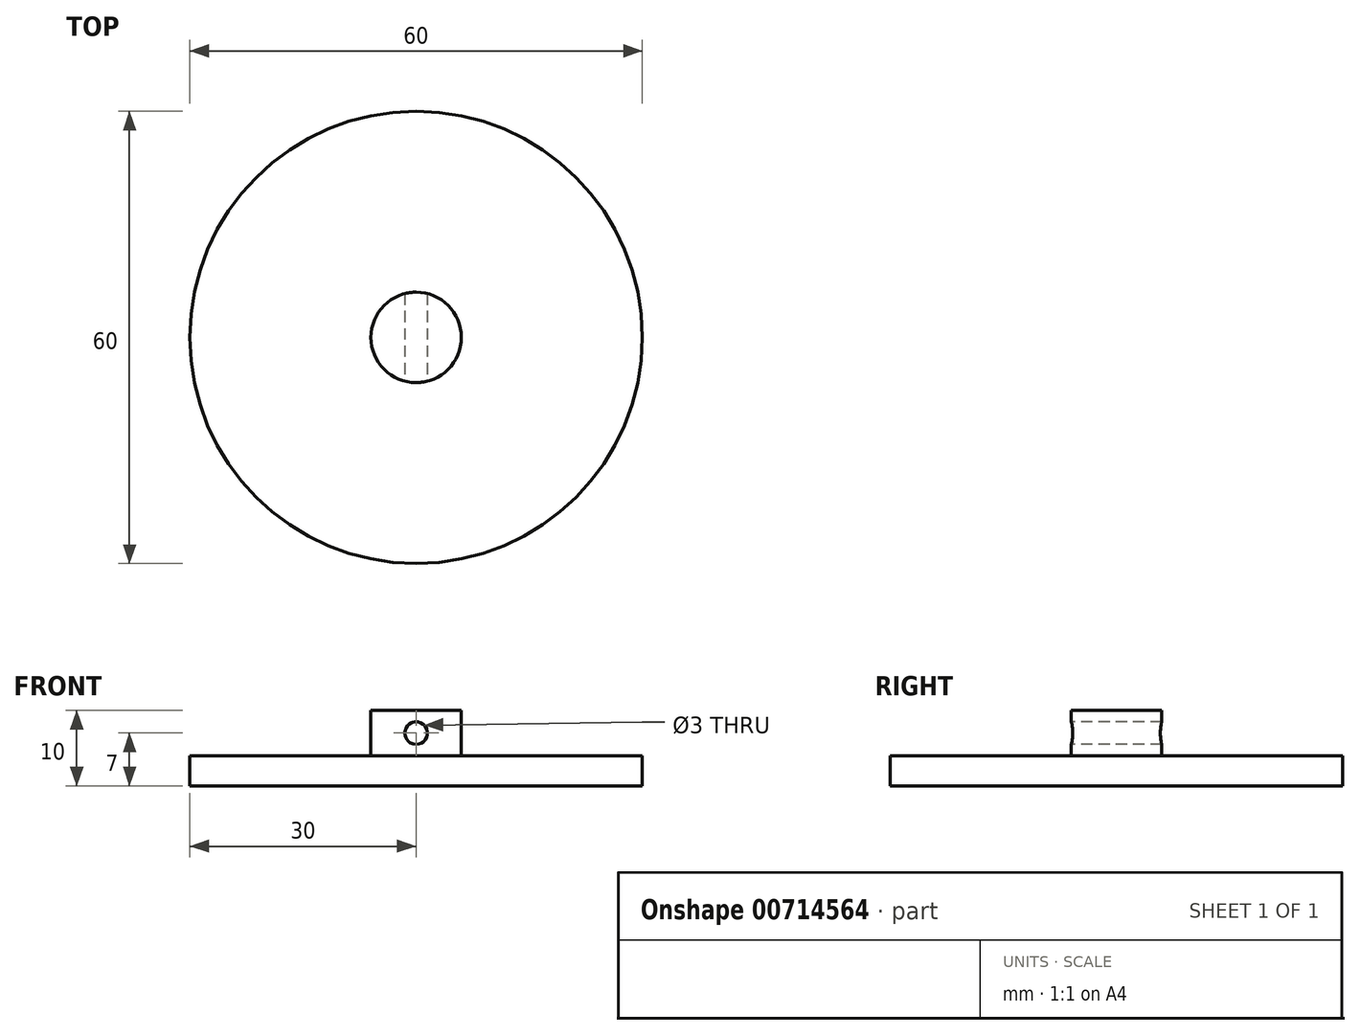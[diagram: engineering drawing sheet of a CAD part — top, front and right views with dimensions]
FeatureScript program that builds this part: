
annotation { "Feature Type Name" : "Feature", "Feature Type Description" : "" }
export const myFeature = defineFeature(function(context is Context, id is Id, definition is map)
    precondition{}
    {
        {
            var Q0;
            Q0=qCreatedBy(makeId("Top.planeOp"),FACE);
            var sketch = newSketch(context, id + "F0", { "sketchPlane" : qUnion([Q0])});
            skCircle(sketch, "E0", {"center": v(0, 0) * mm, "radius": 30 * mm});
            skCircle(sketch, "E1", {"center": v(0, 0) * mm, "radius": 6 * mm});
            skSolve(sketch);
        }
        {
            var Q0;
            Q0 = qSketchRegion(id + "F0", true);
            var Q1;
            Q1=makeQuery(id+"F0.imprint","IMPRINT",FACE,{"disambiguationData":[TD([[makeQuery(id+"F0.imprint","IMPRINT",EDGE,{"derivedFrom":sQuery(id+"F0.wireOp",EDGE,"E1")}),1.0]])]});
            extrude(context, id + "F1", {"entities" : qUnion([Q0, Q1]), "oppositeDirection" : true, "depth" : 4 * mm, "offsetDistance" : 25 * mm});
        }
        {
            var Q0;
            Q0=makeQuery(id+"F0.imprint","IMPRINT",FACE,{"disambiguationData":[TD([[makeQuery(id+"F0.imprint","IMPRINT",EDGE,{"derivedFrom":sQuery(id+"F0.wireOp",EDGE,"E1")}),1.0]])]});
            extrude(context, id + "F2", {"entities" : qUnion([Q0]), "operationType" : NewBodyOperationType.ADD, "depth" : 6 * mm, "offsetDistance" : 25 * mm});
        }
        {
            var Q0;
            Q0=qCreatedBy(makeId("Front.planeOp"),FACE);
            var sketch = newSketch(context, id + "F3", { "sketchPlane" : qUnion([Q0])});
            skCircle(sketch, "E2", {"center": v(0, 3) * mm, "radius": 1.5 * mm});
            skSolve(sketch);
        }
        {
            var Q0;
            Q0 = qSketchRegion(id + "F3", true);
            extrude(context, id + "F4", {"entities" : qUnion([Q0]), "operationType" : NewBodyOperationType.REMOVE, "endBound" : BoundingType.SYMMETRIC, "oppositeDirection" : true, "depth" : 25 * mm, "offsetDistance" : 25 * mm});
        }
    });
